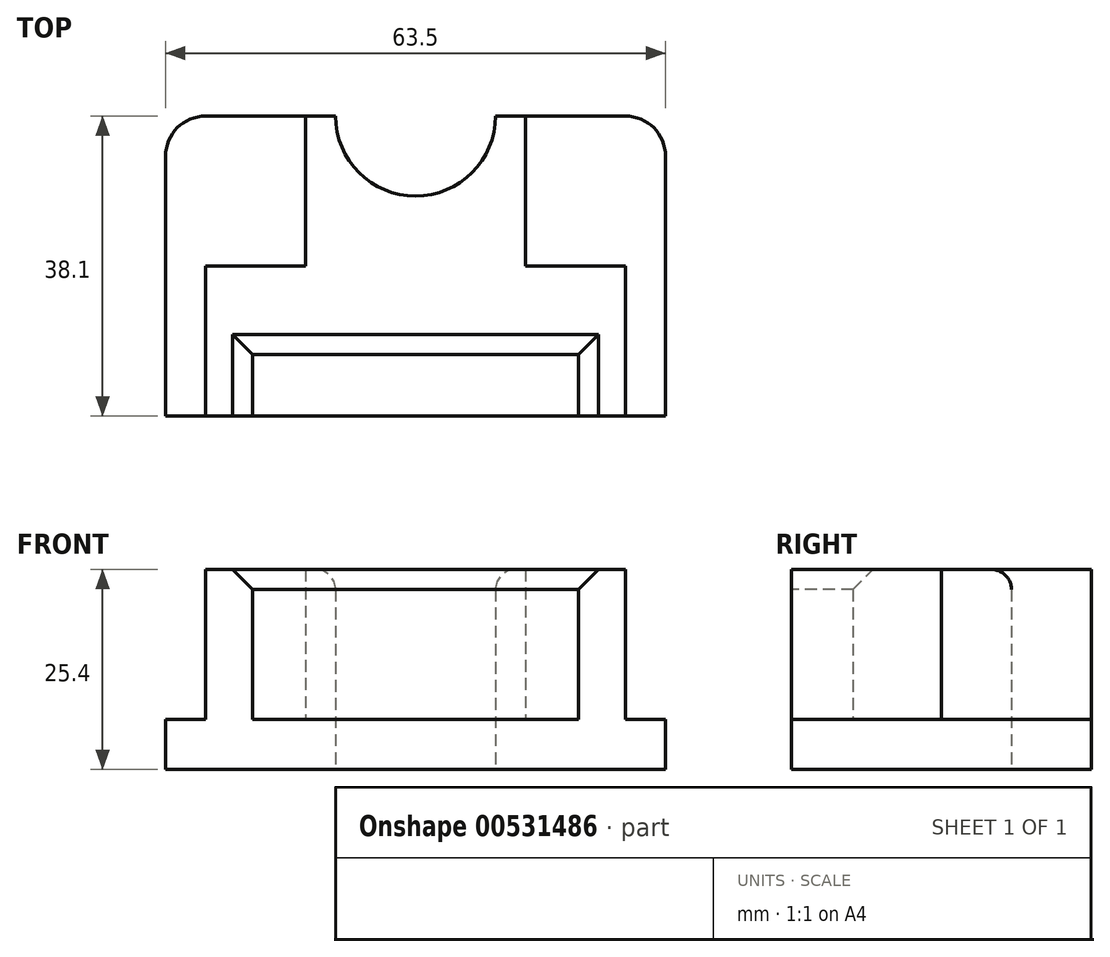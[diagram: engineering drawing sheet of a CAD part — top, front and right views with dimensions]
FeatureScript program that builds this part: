
annotation { "Feature Type Name" : "Feature", "Feature Type Description" : "" }
export const myFeature = defineFeature(function(context is Context, id is Id, definition is map)
    precondition{}
    {
        {
            var Q0;
            Q0=qCreatedBy(makeId("Top.planeOp"),FACE);
            var sketch = newSketch(context, id + "F0", { "sketchPlane" : qUnion([Q0])});
            skLineSegment(sketch, "E0.bottom", {"start": v(31.75, -19.05) * mm, "end": v(-31.75, -19.05) * mm});
            skLineSegment(sketch, "E0.top", {"start": v(31.75, 19.05) * mm, "end": v(-31.75, 19.05) * mm});
            skLineSegment(sketch, "E0.left", {"start": v(31.75, -19.05) * mm, "end": v(31.75, 19.05) * mm});
            skLineSegment(sketch, "E0.right", {"start": v(-31.75, -19.05) * mm, "end": v(-31.75, 19.05) * mm});
            skPoint(sketch, "E0.middle", {"position": v(0, 0) * mm});
            skSolve(sketch);
        }
        {
            var Q0;
            Q0=makeQuery(id+"F0.imprint","IMPRINT",FACE,{"disambiguationData":[TD([[makeQuery(id+"F0.imprint","IMPRINT",EDGE,{"derivedFrom":sQuery(id+"F0.wireOp",EDGE,"E0.bottom")}),-1.0]])]});
            extrude(context, id + "F1", {"entities" : qUnion([Q0]), "depth" : 6.35 * mm, "offsetDistance" : 25.4 * mm});
        }
        {
            var Q0;
            Q0=makeQuery(id+"F1.opExtrude","SWEPT_EDGE",EDGE,{"disambiguationData":[OSD([sQuery(id+"F0.wireOp",EDGE,"E0.top"),sQuery(id+"F0.wireOp",EDGE,"E0.right")])]});
            var Q1;
            Q1=makeQuery(id+"F1.opExtrude","SWEPT_EDGE",EDGE,{"disambiguationData":[OSD([sQuery(id+"F0.wireOp",EDGE,"E0.top"),sQuery(id+"F0.wireOp",EDGE,"E0.left")])]});
            fillet(context, id + "F2", {"entities" : qUnion([Q0, Q1]), "radius" : 5.08 * mm, "tangentPropagation" : true, "allowEdgeOverflow" : false});
        }
        {
            var Q0;
            Q0=makeQuery(id+"F1.opExtrude","CAP_FACE",FACE,{"disambiguationData":[OSD([sQuery(id+"F0.wireOp",EDGE,"E0.bottom"),sQuery(id+"F0.wireOp",EDGE,"E0.top"),sQuery(id+"F0.wireOp",EDGE,"E0.left"),sQuery(id+"F0.wireOp",EDGE,"E0.right")])],"isStart":false});
            var sketch = newSketch(context, id + "F3", { "sketchPlane" : qUnion([Q0])});
            skCircle(sketch, "E1", {"center": v(0, 19.05) * mm, "radius": 10.16 * mm});
            skLineSegment(sketch, "E2", {"start": v(-26.67, 19.05) * mm, "end": v(-26.67, 0) * mm});
            skLineSegment(sketch, "E3", {"start": v(-26.67, 0) * mm, "end": v(-26.67, 0) * mm});
            skLineSegment(sketch, "E4", {"start": v(-26.67, 0) * mm, "end": v(-26.67, -19.05) * mm});
            skLineSegment(sketch, "E5.MirrorCS", {"start": v(26.67, 19.05) * mm, "end": v(26.67, 0) * mm});
            skLineSegment(sketch, "E6.MirrorCS", {"start": v(26.67, 0) * mm, "end": v(26.67, 0) * mm});
            skLineSegment(sketch, "E7.MirrorCS", {"start": v(26.67, 0) * mm, "end": v(26.67, -19.05) * mm});
            skLineSegment(sketch, "E8", {"start": v(-14, 19.05) * mm, "end": v(-14, 0) * mm});
            skLineSegment(sketch, "E9", {"start": v(-14, 0) * mm, "end": v(-26.67, 0) * mm});
            skLineSegment(sketch, "E10.MirrorCS", {"start": v(14, 19.05) * mm, "end": v(14, 0) * mm});
            skLineSegment(sketch, "E11.MirrorCS", {"start": v(14, 0) * mm, "end": v(26.67, 0) * mm});
            skLineSegment(sketch, "E12", {"start": v(-20.7, -19.05) * mm, "end": v(-20.7, -11.22) * mm});
            skLineSegment(sketch, "E13", {"start": v(-20.7, -11.22) * mm, "end": v(0, -11.22) * mm});
            skLineSegment(sketch, "E14.MirrorCS", {"start": v(20.7, -11.22) * mm, "end": v(0, -11.22) * mm});
            skLineSegment(sketch, "E15.MirrorCS", {"start": v(20.7, -19.05) * mm, "end": v(20.7, -11.22) * mm});
            skSolve(sketch);
        }
        {
            var Q0;
            {var subQ7=sQuery(id+"F3.wireOp",EDGE,"E4");Q0=makeQuery(id+"F3.imprint","IMPRINT",FACE,{"disambiguationData":[TD([[makeQuery(id+"F3.imprint","IMPRINT",EDGE,{"derivedFrom":subQ7}),1.0]])]});}
            extrude(context, id + "F4", {"entities" : qUnion([Q0]), "operationType" : NewBodyOperationType.ADD, "depth" : 19.05 * mm, "offsetDistance" : 25.4 * mm});
        }
        {
            var Q0;
            Q0 = qSketchRegion(id + "F3", true);
            extrude(context, id + "F5", {"entities" : qUnion([Q0]), "operationType" : NewBodyOperationType.REMOVE, "oppositeDirection" : true, "depth" : 25.4 * mm, "offsetDistance" : 25.4 * mm});
        }
        {
            var Q0;
            Q0=makeQuery(id+"F4.opExtrude","CAP_EDGE",EDGE,{"disambiguationData":[OSD([sQuery(id+"F3.wireOp",EDGE,"E1")])],"isStart":false});
            fillet(context, id + "F6", {"entities" : qUnion([Q0]), "radius" : 2.54 * mm, "tangentPropagation" : true, "allowEdgeOverflow" : false});
        }
        {
            var Q0;
            Q0=makeQuery(id+"F4.opExtrude","CAP_EDGE",EDGE,{"disambiguationData":[OSD([sQuery(id+"F3.wireOp",EDGE,"E13"),sQuery(id+"F3.wireOp",EDGE,"E14.MirrorCS")])],"isStart":false});
            var Q1;
            Q1=makeQuery(id+"F4.opExtrude","CAP_EDGE",EDGE,{"disambiguationData":[OSD([sQuery(id+"F3.wireOp",EDGE,"E12")])],"isStart":false});
            var Q2;
            Q2=makeQuery(id+"F4.opExtrude","CAP_EDGE",EDGE,{"disambiguationData":[OSD([sQuery(id+"F3.wireOp",EDGE,"E15.MirrorCS")])],"isStart":false});
            chamfer(context, id + "F7", {"entities" : qUnion([Q0, Q1, Q2]), "width" : 2.54 * mm, "tangentPropagation" : true});
        }
    });
